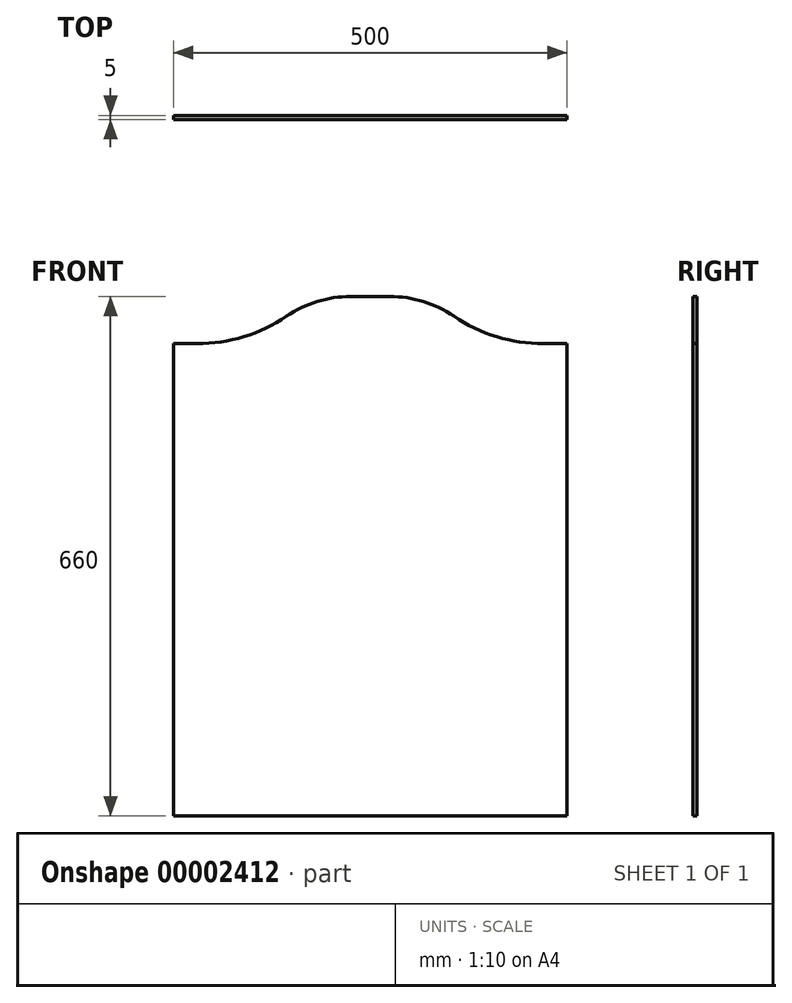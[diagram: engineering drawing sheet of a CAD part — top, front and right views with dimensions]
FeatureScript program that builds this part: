
annotation { "Feature Type Name" : "Feature", "Feature Type Description" : "" }
export const myFeature = defineFeature(function(context is Context, id is Id, definition is map)
    precondition{}
    {
        {
            var Q0;
            Q0=qCreatedBy(makeId("Front.planeOp"),FACE);
            var sketch = newSketch(context, id + "F0", { "sketchPlane" : qUnion([Q0])});
            skLineSegment(sketch, "E0.rect.top", {"start": v(-250, -300) * mm, "end": v(250, -300) * mm});
            skLineSegment(sketch, "E0.rect.left", {"start": v(-250, 300) * mm, "end": v(-250, -300) * mm});
            skLineSegment(sketch, "E0.rect.right", {"start": v(250, 300) * mm, "end": v(250, -300) * mm});
            skPoint(sketch, "E0.rect.middle", {"position": v(0, 0) * mm});
            skLineSegment(sketch, "E1", {"start": v(-250, 300) * mm, "end": v(-220, 300) * mm});
            skLineSegment(sketch, "E2", {"start": v(250, 300) * mm, "end": v(220, 300) * mm});
            skArc(sketch, "E3", {"start": v(-220, 300) * mm, "mid": v(-160.5, 308.95) * mm, "end": v(-106.25, 335) * mm});
            skArc(sketch, "E4", {"start": v(-106.25, 335) * mm, "mid": v(-67.5, 353.6) * mm, "end": v(-25, 360) * mm});
            skArc(sketch, "E5", {"start": v(220, 300) * mm, "mid": v(160.5, 308.95) * mm, "end": v(106.25, 335) * mm});
            skArc(sketch, "E6", {"start": v(106.25, 335) * mm, "mid": v(67.5, 353.6) * mm, "end": v(25, 360) * mm});
            skLineSegment(sketch, "E7", {"start": v(-25, 360) * mm, "end": v(25, 360) * mm});
            skLineSegment(sketch, "E8", {"start": v(0, 615.43) * mm, "end": v(0, -542.29) * mm, "construction": true});
            skSolve(sketch);
        }
        {
            var Q0;
            Q0=makeQuery(id+"F0.imprint","IMPRINT",FACE,{"disambiguationData":[TD([[makeQuery(id+"F0.imprint","IMPRINT",EDGE,{"derivedFrom":sQuery(id+"F0.wireOp",EDGE,"E0.rect.top")}),1.0]])]});
            extrude(context, id + "F1", {"entities" : qUnion([Q0]), "depth" : 5 * mm});
        }
    });
